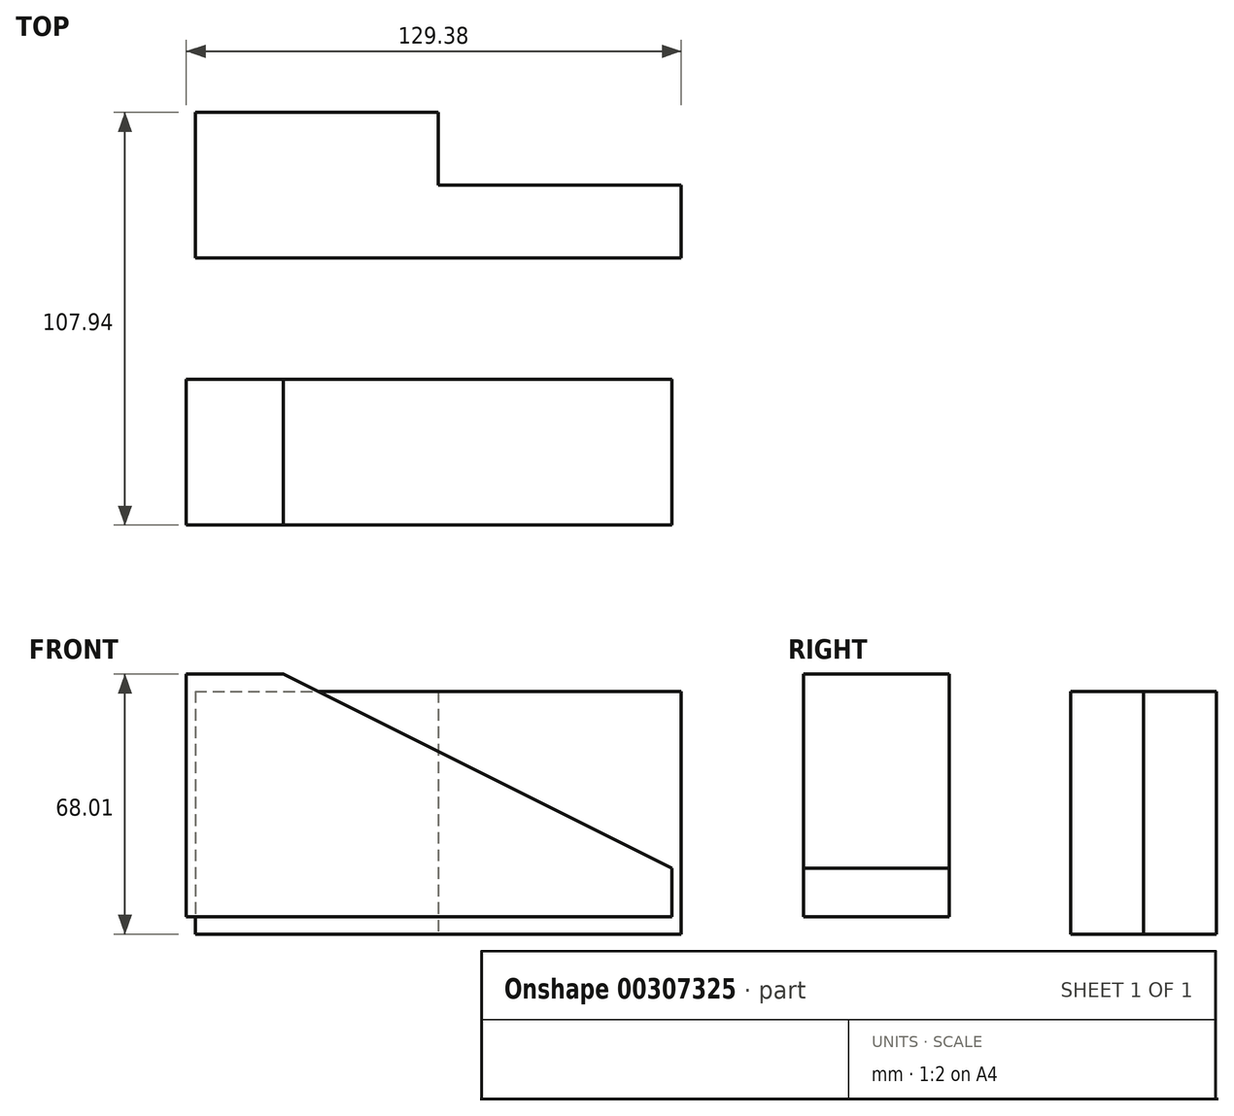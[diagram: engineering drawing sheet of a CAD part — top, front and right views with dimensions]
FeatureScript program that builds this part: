
annotation { "Feature Type Name" : "Feature", "Feature Type Description" : "" }
export const myFeature = defineFeature(function(context is Context, id is Id, definition is map)
    precondition{}
    {
        {
            var Q0;
            Q0=qCreatedBy(makeId("Front.planeOp"),FACE);
            var sketch = newSketch(context, id + "F0", { "sketchPlane" : qUnion([Q0])});
            skLineSegment(sketch, "E0", {"start": v(-56.14, 68.01) * mm, "end": v(-30.74, 68.01) * mm});
            skLineSegment(sketch, "E1", {"start": v(-56.14, 68.01) * mm, "end": v(-56.14, 4.51) * mm});
            skLineSegment(sketch, "E2", {"start": v(-56.14, 4.51) * mm, "end": v(70.86, 4.51) * mm});
            skLineSegment(sketch, "E3", {"start": v(70.86, 4.51) * mm, "end": v(70.86, 17.21) * mm});
            skLineSegment(sketch, "E4", {"start": v(-30.74, 68.01) * mm, "end": v(70.86, 17.21) * mm});
            skSolve(sketch);
        }
        {
            var Q0;
            Q0=makeQuery(id+"F0.imprint","IMPRINT",FACE,{"disambiguationData":[TD([[makeQuery(id+"F0.imprint","IMPRINT",EDGE,{"derivedFrom":sQuery(id+"F0.wireOp",EDGE,"E0")}),-1.0]])]});
            extrude(context, id + "F1", {"entities" : qUnion([Q0]), "depth" : 38.1 * mm});
        }
        {
            var Q0;
            Q0=qCreatedBy(makeId("Top.planeOp"),FACE);
            var sketch = newSketch(context, id + "F2", { "sketchPlane" : qUnion([Q0])});
            skLineSegment(sketch, "E5", {"start": v(-53.76, 69.84) * mm, "end": v(9.74, 69.84) * mm});
            skLineSegment(sketch, "E6", {"start": v(9.74, 69.84) * mm, "end": v(9.74, 50.79) * mm});
            skLineSegment(sketch, "E7", {"start": v(9.74, 50.79) * mm, "end": v(73.24, 50.79) * mm});
            skLineSegment(sketch, "E8", {"start": v(-53.76, 69.84) * mm, "end": v(-53.76, 31.74) * mm});
            skLineSegment(sketch, "E9", {"start": v(-53.76, 31.74) * mm, "end": v(73.24, 31.74) * mm});
            skLineSegment(sketch, "E10", {"start": v(73.24, 50.79) * mm, "end": v(73.24, 31.74) * mm});
            skSolve(sketch);
        }
        {
            var Q0;
            Q0 = qSketchRegion(id + "F2", true);
            extrude(context, id + "F3", {"entities" : qUnion([Q0]), "depth" : 63.5 * mm});
        }
    });
